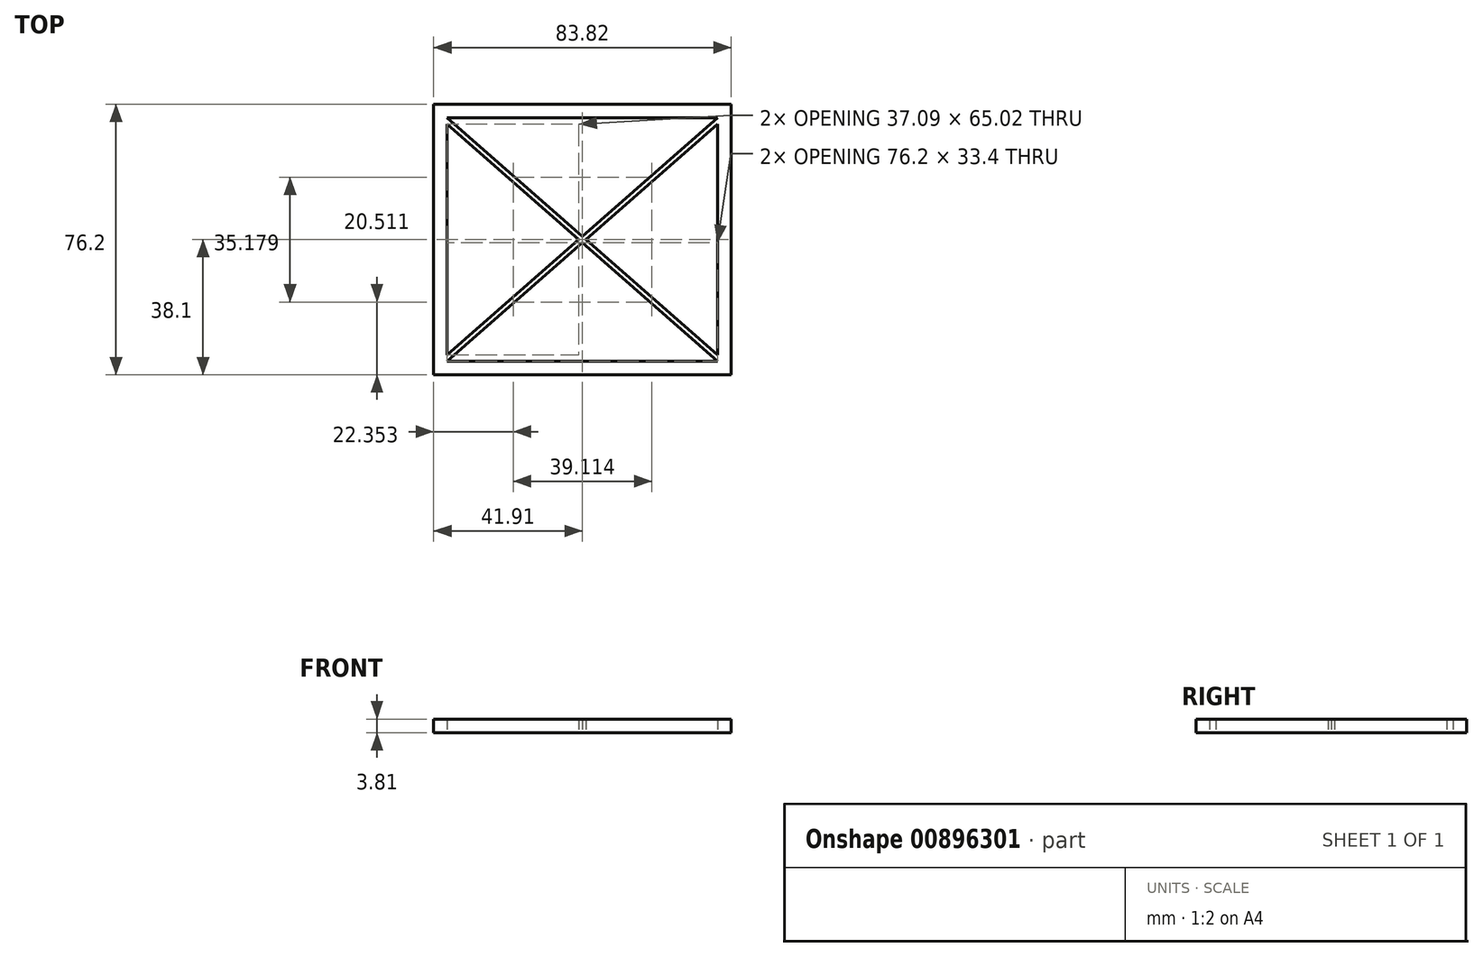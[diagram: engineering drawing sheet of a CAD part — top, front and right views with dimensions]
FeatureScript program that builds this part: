
annotation { "Feature Type Name" : "Feature", "Feature Type Description" : "" }
export const myFeature = defineFeature(function(context is Context, id is Id, definition is map)
    precondition{}
    {
        {
            var Q0;
            Q0=qCreatedBy(makeId("Top.planeOp"),FACE);
            var sketch = newSketch(context, id + "F0", { "sketchPlane" : qUnion([Q0])});
            skLineSegment(sketch, "E0.bottom", {"start": v(-41.9, -38.1) * mm, "end": v(41.91, -38.1) * mm});
            skLineSegment(sketch, "E0.top", {"start": v(-41.91, 38.1) * mm, "end": v(41.9, 38.1) * mm});
            skLineSegment(sketch, "E0.left", {"start": v(-41.9, -38.1) * mm, "end": v(-41.91, 38.1) * mm});
            skPoint(sketch, "E0.middle", {"position": v(0, 0) * mm});
            skLineSegment(sketch, "E1.bottom", {"start": v(-38.1, 34.3) * mm, "end": v(38.1, 34.3) * mm});
            skLineSegment(sketch, "E1.top", {"start": v(-38.1, -34.3) * mm, "end": v(38.1, -34.3) * mm});
            skLineSegment(sketch, "E2", {"start": v(38.1, -34.3) * mm, "end": v(38.1, -32.51) * mm});
            skLineSegment(sketch, "E3", {"start": v(-38.1, -34.3) * mm, "end": v(-38.1, -32.51) * mm});
            skLineSegment(sketch, "E4", {"start": v(38.1, 34.3) * mm, "end": v(38.1, 32.51) * mm});
            skLineSegment(sketch, "E5", {"start": v(-38.1, 34.3) * mm, "end": v(-38.1, 32.51) * mm});
            skLineSegment(sketch, "E6", {"start": v(38.1, 32.51) * mm, "end": v(38.1, -32.51) * mm});
            skLineSegment(sketch, "E7", {"start": v(-38.1, 32.51) * mm, "end": v(-38.1, -32.51) * mm});
            skLineSegment(sketch, "E8", {"start": v(0, 0.89) * mm, "end": v(-38.1, 34.3) * mm});
            skLineSegment(sketch, "E9", {"start": v(-1.01, 0) * mm, "end": v(-38.1, 32.51) * mm});
            skLineSegment(sketch, "E10", {"start": v(0, 0.89) * mm, "end": v(38.1, 34.3) * mm});
            skLineSegment(sketch, "E11", {"start": v(38.1, 32.51) * mm, "end": v(1.01, 0) * mm});
            skLineSegment(sketch, "E12", {"start": v(1.01, 0) * mm, "end": v(38.1, -32.51) * mm});
            skLineSegment(sketch, "E13", {"start": v(38.1, -34.3) * mm, "end": v(0, -0.89) * mm});
            skLineSegment(sketch, "E14", {"start": v(0, -0.89) * mm, "end": v(-38.1, -34.3) * mm});
            skLineSegment(sketch, "E15", {"start": v(-38.1, -32.51) * mm, "end": v(-1.01, 0) * mm});
            skLineSegment(sketch, "E16", {"start": v(41.91, -38.1) * mm, "end": v(41.91, -34.13) * mm});
            skLineSegment(sketch, "E17", {"start": v(41.91, -34.13) * mm, "end": v(41.91, -30.16) * mm});
            skLineSegment(sketch, "E18", {"start": v(41.91, -30.16) * mm, "end": v(41.91, -26.2) * mm});
            skLineSegment(sketch, "E19", {"start": v(41.91, -26.2) * mm, "end": v(41.91, -22.22) * mm});
            skLineSegment(sketch, "E20", {"start": v(41.91, -22.22) * mm, "end": v(41.91, 38.1) * mm});
            skSolve(sketch);
        }
        {
            var Q0;
            Q0 = qSketchRegion(id + "F0", true);
            var Q1;
            Q1=makeQuery(id+"F0.imprint","IMPRINT",FACE,{"disambiguationData":[TD([[makeQuery(id+"F0.imprint","IMPRINT",EDGE,{"derivedFrom":sQuery(id+"F0.wireOp",EDGE,"E2")}),1.0]])]});
            extrude(context, id + "F1", {"entities" : qUnion([Q0, Q1]), "depth" : 3.8 * mm, "offsetDistance" : 25.4 * mm});
        }
    });
